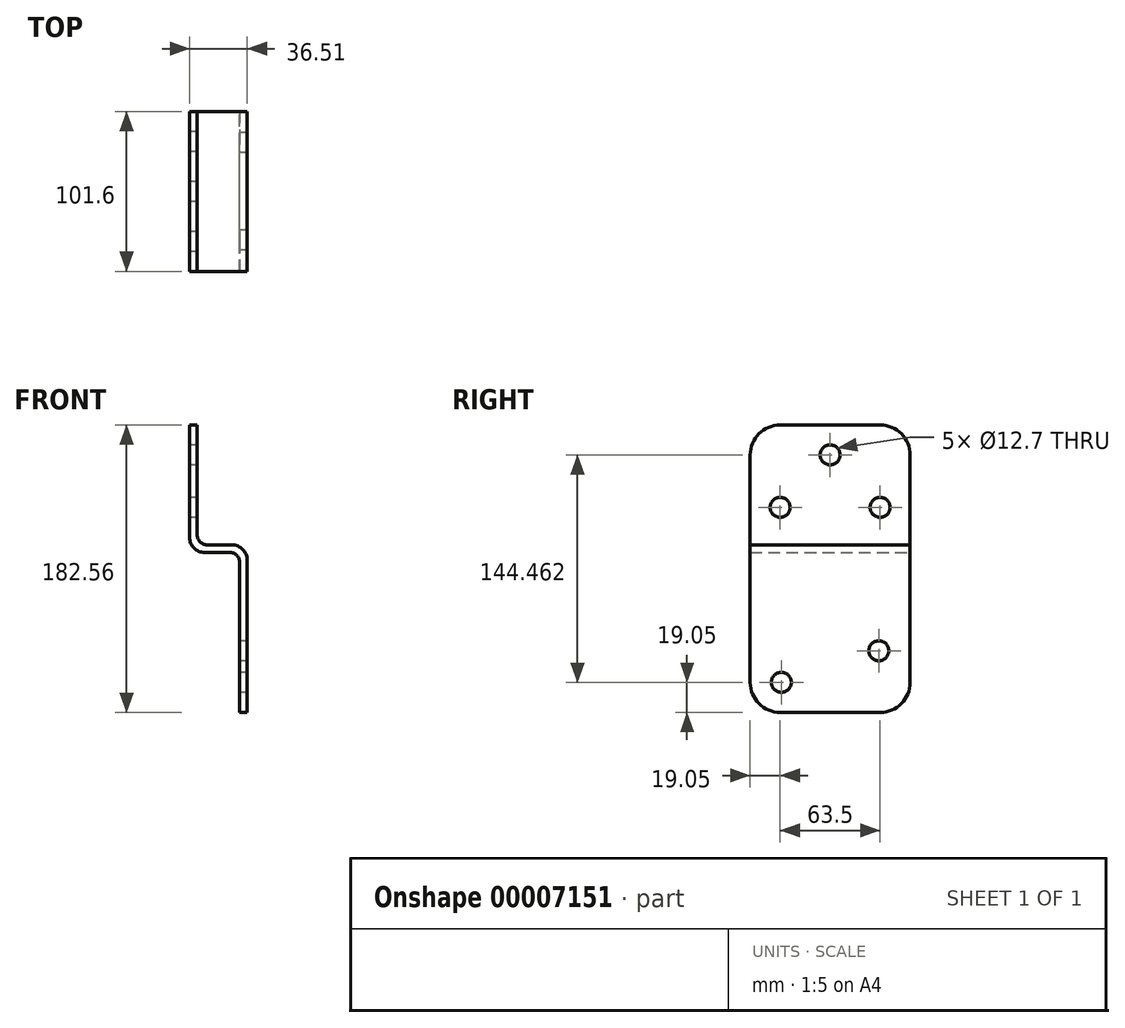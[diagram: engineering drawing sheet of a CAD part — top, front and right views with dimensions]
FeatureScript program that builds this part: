
annotation { "Feature Type Name" : "Feature", "Feature Type Description" : "" }
export const myFeature = defineFeature(function(context is Context, id is Id, definition is map)
    precondition{}
    {
        {
            var Q0;
            Q0=qCreatedBy(makeId("Front.planeOp"),FACE);
            var sketch = newSketch(context, id + "F0", { "sketchPlane" : qUnion([Q0])});
            skLineSegment(sketch, "E0", {"start": v(0, 0) * mm, "end": v(0, 95.25) * mm});
            skLineSegment(sketch, "E1", {"start": v(-6.35, 101.6) * mm, "end": v(-22.23, 101.6) * mm});
            skLineSegment(sketch, "E2", {"start": v(-31.75, 111.13) * mm, "end": v(-31.75, 182.56) * mm});
            skLineSegment(sketch, "E3", {"start": v(-31.75, 182.56) * mm, "end": v(-26.99, 182.56) * mm});
            skLineSegment(sketch, "E4", {"start": v(-26.99, 182.56) * mm, "end": v(-26.99, 112.71) * mm});
            skLineSegment(sketch, "E5", {"start": v(-20.64, 106.36) * mm, "end": v(-4.76, 106.36) * mm});
            skLineSegment(sketch, "E6", {"start": v(4.76, 96.84) * mm, "end": v(4.76, 0) * mm});
            skLineSegment(sketch, "E7", {"start": v(4.76, 0) * mm, "end": v(0, 0) * mm});
            skLineSegment(sketch, "E8", {"start": v(-11.11, 106.36) * mm, "end": v(-11.11, 101.6) * mm, "construction": true});
            skPoint(sketch, "E9.visualSharp", {"position": v(0, 101.6) * mm});
            skArc(sketch, "E9.filletArc", {"start": v(0, 95.25) * mm, "mid": v(-1.86, 99.74) * mm, "end": v(-6.35, 101.6) * mm});
            skPoint(sketch, "E10.visualSharp", {"position": v(-26.99, 106.36) * mm});
            skArc(sketch, "E10.filletArc", {"start": v(-26.99, 112.71) * mm, "mid": v(-25.13, 108.22) * mm, "end": v(-20.64, 106.36) * mm});
            skPoint(sketch, "E11.visualSharp", {"position": v(-31.75, 101.6) * mm});
            skArc(sketch, "E11.filletArc", {"start": v(-31.75, 111.13) * mm, "mid": v(-28.96, 104.39) * mm, "end": v(-22.23, 101.6) * mm});
            skPoint(sketch, "E12.visualSharp", {"position": v(4.76, 106.36) * mm});
            skArc(sketch, "E12.filletArc", {"start": v(4.76, 96.84) * mm, "mid": v(1.97, 103.57) * mm, "end": v(-4.76, 106.36) * mm});
            skSolve(sketch);
        }
        {
            var Q0;
            Q0=makeQuery(id+"F0.imprint","IMPRINT",FACE,{"disambiguationData":[TD([[makeQuery(id+"F0.imprint","IMPRINT",EDGE,{"derivedFrom":sQuery(id+"F0.wireOp",EDGE,"E0")}),-1.0]])]});
            extrude(context, id + "F1", {"entities" : qUnion([Q0]), "depth" : 101.6 * mm});
        }
        {
            var Q0;
            Q0=makeQuery(id+"F1.opExtrude","SWEPT_FACE",FACE,{"disambiguationData":[OSD([sQuery(id+"F0.wireOp",EDGE,"E0")])]});
            var sketch = newSketch(context, id + "F2", { "sketchPlane" : qUnion([Q0])});
            skLineSegment(sketch, "E13", {"start": v(19.84, 39.13) * mm, "end": v(81.76, 19.05) * mm, "construction": true});
            skCircle(sketch, "E14", {"center": v(19.84, 39.13) * mm, "radius": 6.35 * mm});
            skCircle(sketch, "E15", {"center": v(81.76, 19.05) * mm, "radius": 6.35 * mm});
            skLineSegment(sketch, "E16", {"start": v(19.84, 39.13) * mm, "end": v(0, 39.13) * mm, "construction": true});
            skLineSegment(sketch, "E17", {"start": v(81.76, 19.05) * mm, "end": v(101.6, 19.05) * mm, "construction": true});
            skLineSegment(sketch, "E18", {"start": v(81.76, 19.05) * mm, "end": v(81.76, 0) * mm, "construction": true});
            skSolve(sketch);
        }
        {
            var Q0;
            Q0=makeQuery(id+"F1.opExtrude","CAP_EDGE",EDGE,{"disambiguationData":[OSD([sQuery(id+"F0.wireOp",EDGE,"E3")])],"isStart":false});
            var Q1;
            Q1=makeQuery(id+"F1.opExtrude","CAP_EDGE",EDGE,{"disambiguationData":[OSD([sQuery(id+"F0.wireOp",EDGE,"E3")])],"isStart":true});
            var Q2;
            Q2=makeQuery(id+"F1.opExtrude","CAP_EDGE",EDGE,{"disambiguationData":[OSD([sQuery(id+"F0.wireOp",EDGE,"E7")])],"isStart":true});
            var Q3;
            Q3=makeQuery(id+"F1.opExtrude","CAP_EDGE",EDGE,{"disambiguationData":[OSD([sQuery(id+"F0.wireOp",EDGE,"E7")])],"isStart":false});
            fillet(context, id + "F3", {"entities" : qUnion([Q0, Q1, Q2, Q3]), "radius" : 19.05 * mm, "tangentPropagation" : true, "allowEdgeOverflow" : false});
        }
        {
            var Q0;
            Q0=makeQuery(id+"F1.opExtrude","SWEPT_FACE",FACE,{"disambiguationData":[OSD([sQuery(id+"F0.wireOp",EDGE,"E2")])]});
            var sketch = newSketch(context, id + "F4", { "sketchPlane" : qUnion([Q0])});
            skLineSegment(sketch, "E19", {"start": v(19.05, 130.18) * mm, "end": v(50.8, 163.51) * mm, "construction": true});
            skLineSegment(sketch, "E20", {"start": v(50.8, 163.51) * mm, "end": v(82.55, 130.18) * mm, "construction": true});
            skLineSegment(sketch, "E21", {"start": v(82.55, 130.18) * mm, "end": v(19.05, 130.18) * mm, "construction": true});
            skLineSegment(sketch, "E22", {"start": v(50.8, 163.51) * mm, "end": v(50.8, 182.56) * mm, "construction": true});
            skLineSegment(sketch, "E23", {"start": v(50.8, 130.18) * mm, "end": v(50.8, 111.13) * mm, "construction": true});
            skLineSegment(sketch, "E24", {"start": v(82.55, 130.18) * mm, "end": v(101.6, 130.18) * mm, "construction": true});
            skCircle(sketch, "E25", {"center": v(50.8, 163.51) * mm, "radius": 6.35 * mm});
            skCircle(sketch, "E26", {"center": v(82.55, 130.18) * mm, "radius": 6.35 * mm});
            skCircle(sketch, "E27", {"center": v(19.05, 130.18) * mm, "radius": 6.35 * mm});
            skSolve(sketch);
        }
        {
            var Q0;
            Q0 = qSketchRegion(id + "F4", true);
            extrude(context, id + "F5", {"entities" : qUnion([Q0]), "operationType" : NewBodyOperationType.REMOVE, "endBound" : BoundingType.THROUGH_ALL, "oppositeDirection" : true, "depth" : 25.4 * mm});
        }
        {
            var Q0;
            Q0 = qSketchRegion(id + "F2", true);
            extrude(context, id + "F6", {"entities" : qUnion([Q0]), "operationType" : NewBodyOperationType.REMOVE, "endBound" : BoundingType.THROUGH_ALL, "oppositeDirection" : true, "depth" : 25.4 * mm});
        }
    });
